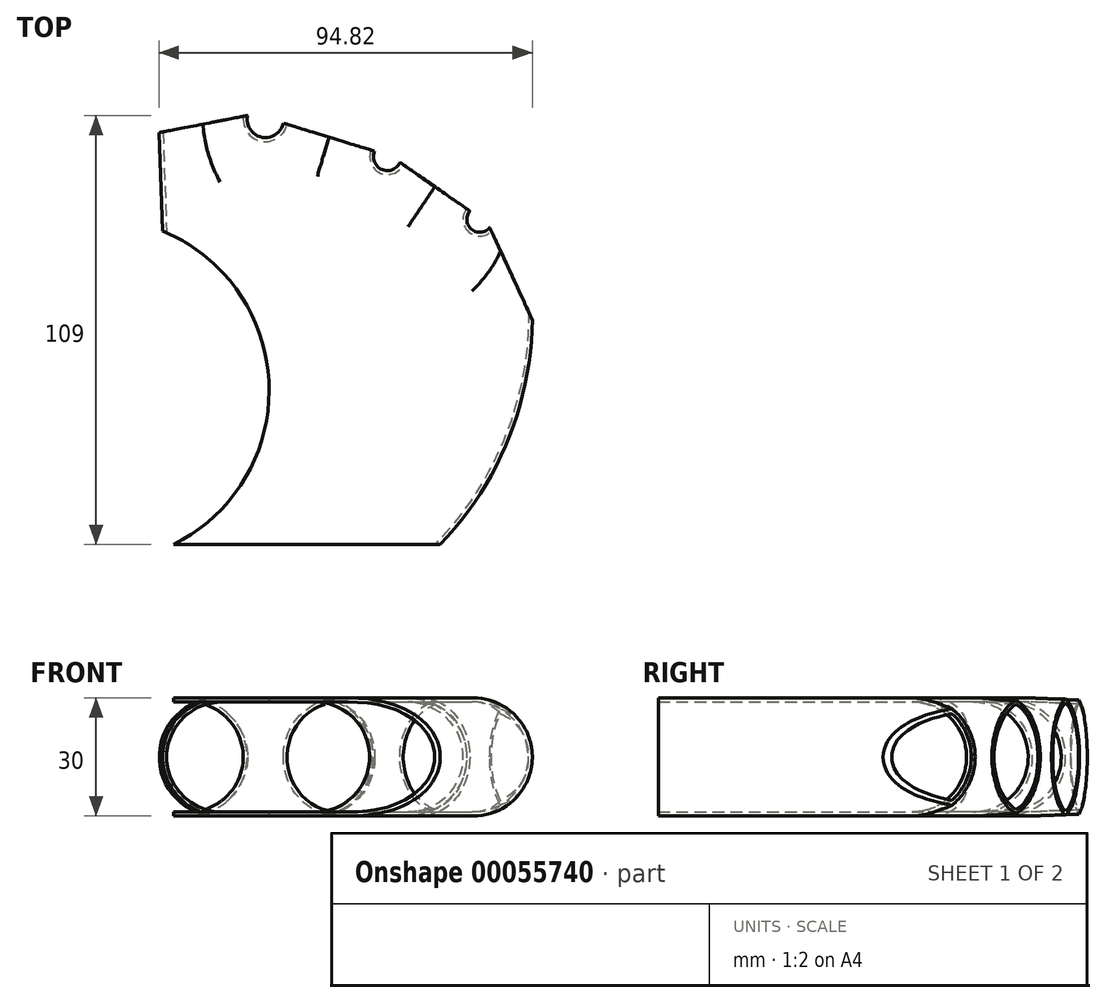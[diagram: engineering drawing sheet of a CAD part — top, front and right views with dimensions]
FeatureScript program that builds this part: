
annotation { "Feature Type Name" : "Feature", "Feature Type Description" : "" }
export const myFeature = defineFeature(function(context is Context, id is Id, definition is map)
    precondition{}
    {
        {
            var Q0;
            Q0=qCreatedBy(makeId("Top.planeOp"),FACE);
            var sketch = newSketch(context, id + "F0", { "sketchPlane" : qUnion([Q0])});
            skLineSegment(sketch, "E0", {"start": v(-125.98, -58.16) * mm, "end": v(-58.28, -58.16) * mm});
            skLineSegment(sketch, "E1", {"start": v(-45.7, 22.36) * mm, "end": v(-34.9, -1.06) * mm});
            skLineSegment(sketch, "E2", {"start": v(-50.78, 26.59) * mm, "end": v(-68.52, 38.9) * mm});
            skLineSegment(sketch, "E3", {"start": v(-74.92, 41.75) * mm, "end": v(-98.15, 48.88) * mm});
            skPoint(sketch, "E4.endSnap0", {"position": v(-112.07, -4.64) * mm});
            skLineSegment(sketch, "E5", {"start": v(-107.24, 50.84) * mm, "end": v(-129.72, 46.47) * mm});
            skArc(sketch, "E6", {"start": v(-58.28, -58.16) * mm, "mid": v(-41.16, -31.83) * mm, "end": v(-34.9, -1.06) * mm});
            skArc(sketch, "E7", {"start": v(-125.98, -58.16) * mm, "mid": v(-101.79, -17.43) * mm, "end": v(-128.83, 21.47) * mm});
            skPoint(sketch, "E7.first.point", {"position": v(-128.83, 21.47) * mm});
            skPoint(sketch, "E7.third.point", {"position": v(-102.34, -11.9) * mm});
            skArc(sketch, "E8", {"start": v(-107.24, 50.84) * mm, "mid": v(-103.68, 45.32) * mm, "end": v(-98.15, 48.88) * mm});
            skArc(sketch, "E9", {"start": v(-74.92, 41.75) * mm, "mid": v(-73.14, 37.13) * mm, "end": v(-68.52, 38.9) * mm});
            skArc(sketch, "E10", {"start": v(-50.78, 26.59) * mm, "mid": v(-50.36, 21.94) * mm, "end": v(-45.7, 22.36) * mm});
            skLineSegment(sketch, "E11", {"start": v(-129.72, 46.47) * mm, "end": v(-128.83, 21.47) * mm});
            skSolve(sketch);
        }
        {
            var Q0;
            Q0=makeQuery(id+"F0.imprint","IMPRINT",FACE,{"disambiguationData":[TD([[makeQuery(id+"F0.imprint","IMPRINT",EDGE,{"derivedFrom":sQuery(id+"F0.wireOp",EDGE,"E0")}),1.0]])]});
            extrude(context, id + "F1", {"entities" : qUnion([Q0]), "depth" : 30 * mm});
        }
        {
            var Q0;
            Q0=makeQuery(id+"F1.opExtrude","CAP_EDGE",EDGE,{"disambiguationData":[OSD([sQuery(id+"F0.wireOp",EDGE,"E8")])],"isStart":false});
            var Q1;
            Q1=makeQuery(id+"F1.opExtrude","CAP_EDGE",EDGE,{"disambiguationData":[OSD([sQuery(id+"F0.wireOp",EDGE,"E11")])],"isStart":false});
            var Q2;
            Q2=makeQuery(id+"F1.opExtrude","CAP_EDGE",EDGE,{"disambiguationData":[OSD([sQuery(id+"F0.wireOp",EDGE,"E9")])],"isStart":false});
            var Q3;
            Q3=makeQuery(id+"F1.opExtrude","CAP_EDGE",EDGE,{"disambiguationData":[OSD([sQuery(id+"F0.wireOp",EDGE,"E10")])],"isStart":false});
            var Q4;
            Q4=makeQuery(id+"F1.opExtrude","CAP_EDGE",EDGE,{"disambiguationData":[OSD([sQuery(id+"F0.wireOp",EDGE,"E8")])],"isStart":true});
            var Q5;
            Q5=makeQuery(id+"F1.opExtrude","CAP_EDGE",EDGE,{"disambiguationData":[OSD([sQuery(id+"F0.wireOp",EDGE,"E9")])],"isStart":true});
            var Q6;
            Q6=makeQuery(id+"F1.opExtrude","CAP_EDGE",EDGE,{"disambiguationData":[OSD([sQuery(id+"F0.wireOp",EDGE,"E10")])],"isStart":true});
            var Q7;
            Q7=makeQuery(id+"F1.opExtrude","CAP_EDGE",EDGE,{"disambiguationData":[OSD([sQuery(id+"F0.wireOp",EDGE,"E11")])],"isStart":true});
            var Q8;
            Q8=makeQuery(id+"F1.opExtrude","CAP_EDGE",EDGE,{"disambiguationData":[OSD([sQuery(id+"F0.wireOp",EDGE,"E6")])],"isStart":true});
            var Q9;
            Q9=makeQuery(id+"F1.opExtrude","CAP_EDGE",EDGE,{"disambiguationData":[OSD([sQuery(id+"F0.wireOp",EDGE,"E6")])],"isStart":false});
            fillet(context, id + "F2", {"entities" : qUnion([Q0, Q1, Q2, Q3, Q4, Q5, Q6, Q7, Q8, Q9]), "radius" : 15 * mm, "tangentPropagation" : true, "allowEdgeOverflow" : false});
        }
        {
            var Q0;
            Q0=makeQuery(id+"F1.opExtrude","SWEPT_FACE",FACE,{"disambiguationData":[OSD([sQuery(id+"F0.wireOp",EDGE,"E7")])]});
            var Q1;
            Q1=makeQuery(id+"F1.opExtrude","SWEPT_FACE",FACE,{"disambiguationData":[OSD([sQuery(id+"F0.wireOp",EDGE,"E0")])]});
            var Q2;
            Q2=makeQuery(id+"F1.opExtrude","SWEPT_FACE",FACE,{"disambiguationData":[OSD([sQuery(id+"F0.wireOp",EDGE,"E1")])]});
            var Q3;
            Q3=makeQuery(id+"F1.opExtrude","SWEPT_FACE",FACE,{"disambiguationData":[OSD([sQuery(id+"F0.wireOp",EDGE,"E2")])]});
            var Q4;
            Q4=makeQuery(id+"F1.opExtrude","SWEPT_FACE",FACE,{"disambiguationData":[OSD([sQuery(id+"F0.wireOp",EDGE,"E3")])]});
            var Q5;
            Q5=makeQuery(id+"F1.opExtrude","SWEPT_FACE",FACE,{"disambiguationData":[OSD([sQuery(id+"F0.wireOp",EDGE,"E5")])]});
            shell(context, id + "F3", {"entities" : qUnion([Q0, Q1, Q2, Q3, Q4, Q5]), "thickness" : 1 * mm});
        }
    });
